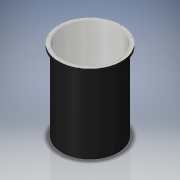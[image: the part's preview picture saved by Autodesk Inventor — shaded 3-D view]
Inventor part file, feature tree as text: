
AUTODESK INVENTOR PART (.ipt)
format: ipt  version: 2018 (Build 220112000, 112)  size: 184,320 bytes
history: native  units: in
note: dims shown in document units (in); Inventor stores cm internally (conversion verified against a paired STEP export)
features: sketch x5, extrude x4, hole x1, pattern_circular x1, fillet x1
ambient origin geometry x8: Origin, YZ Plane, XZ Plane, XY Plane, X Axis, Y Axis, Z Axis, Center Point
bodies: Solid1 (feature_tree)
feature tree (12):
  extrude  "Extrusion1"  Depth=19.125in
  extrude  "Extrusion2"  Depth=1.0in
  hole  "Hole1"  [1 undecoded]
  pattern_circular  "Circular Pattern1"  Count=12 Angle=360.0deg
  extrude  "Extrusion3"  Depth=0.25in
  extrude  "Extrusion6"  Depth=0.25in
  fillet  "Fillet1"  Radius=26.75in
  sketch  "Sketch1"  dims[d0=21.5in d1=19.125in]
  sketch  "Sketch2"  dims[d2=1.0in d3=0.0in d4=19.5in]
  sketch  "Sketch3"  dims[d5=19.875in d6=0.125in d7=0.0in]
  sketch  "Sketch4"  dims[d8=10.4429in]
  sketch  "Sketch8"  dims[d9=0.272in d10=0.63in d11=0.375in d12=0.25in d13=0.5635in d14=0.831in d15=0.8108in d16=4.7244in d17=360.0deg d19=19.125in d20=19.375in d21=26.75in d22=0.0in d45=19.375in d46=0.25in d47=0.0in d48=0.25in]
note: 1 required parameter value undecoded (feature->parameter linkage not recoverable at this tier; creation-order binding heuristic only, values carry confidence <= 0.55)
